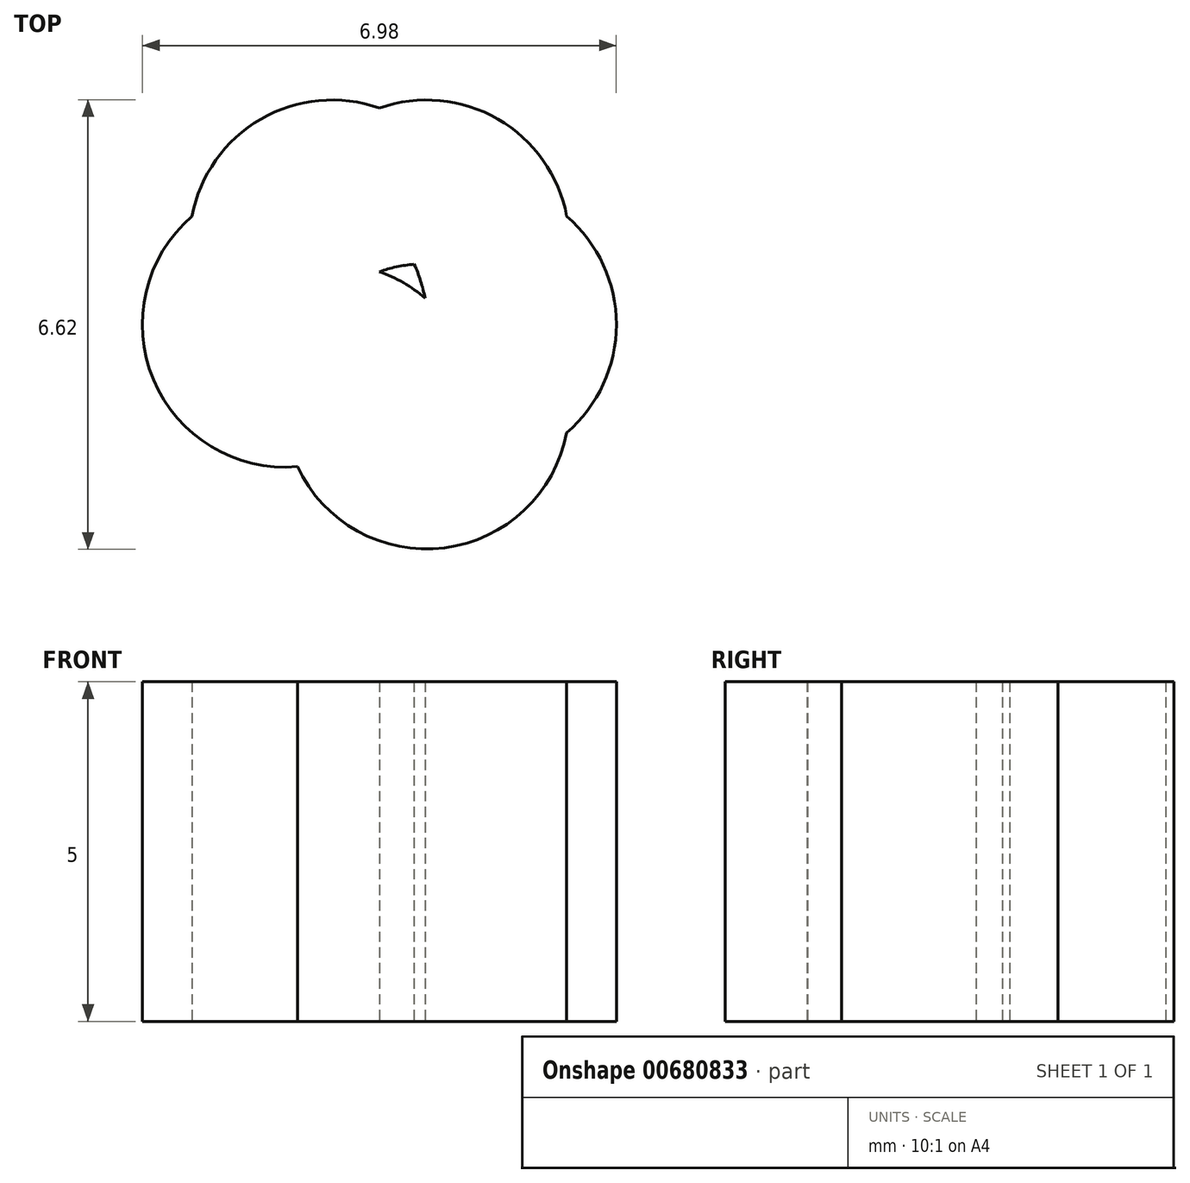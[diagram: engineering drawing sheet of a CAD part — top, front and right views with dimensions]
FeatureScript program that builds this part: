
annotation { "Feature Type Name" : "Feature", "Feature Type Description" : "" }
export const myFeature = defineFeature(function(context is Context, id is Id, definition is map)
    precondition{}
    {
        {
            var Q0;
            Q0=qCreatedBy(makeId("Top.planeOp"),FACE);
            var sketch = newSketch(context, id + "F0", { "sketchPlane" : qUnion([Q0])});
            skCircle(sketch, "E0", {"center": v(0, 0) * mm, "radius": 3.5 * mm});
            skCircle(sketch, "E1", {"center": v(1.4, 0) * mm, "radius": 2.1 * mm});
            skCircle(sketch, "E2.1.0", {"center": v(0.7, 1.2) * mm, "radius": 2.1 * mm});
            skCircle(sketch, "E2.2.0", {"center": v(-0.7, 1.2) * mm, "radius": 2.1 * mm});
            skCircle(sketch, "E2.3.0", {"center": v(-1.4, 0) * mm, "radius": 2.1 * mm});
            skCircle(sketch, "E2.4.0", {"center": v(-0.7, -1.2) * mm, "radius": 2.1 * mm});
            skCircle(sketch, "E2.5.0", {"center": v(0.7, -1.2) * mm, "radius": 2.1 * mm});
            skSolve(sketch);
        }
        {
            var Q0;
            {var subQ0=sQuery(id+"F0.wireOp",EDGE,"E2.2.0");var subQ1=sQuery(id+"F0.wireOp",EDGE,"E1");var subQ2=makeQuery(id+"F0.imprint","INTERSECT",VERTEX,{"disambiguationData":[OD(0.0)],"derivedFrom":[subQ1,subQ0]});Q0=makeQuery(id+"F0.imprint","IMPRINT",FACE,{"disambiguationData":[TD([[makeQuery(id+"F0.imprint","IMPRINT",EDGE,{"disambiguationData":[TD([[subQ2,-1.0]])],"derivedFrom":subQ1}),-1.0]])]});}
            var Q1;
            {var subQ0=sQuery(id+"F0.wireOp",EDGE,"E2.3.0");var subQ1=sQuery(id+"F0.wireOp",EDGE,"E2.1.0");var subQ2=makeQuery(id+"F0.imprint","INTERSECT",VERTEX,{"disambiguationData":[OD(0.0)],"derivedFrom":[subQ1,subQ0]});Q1=makeQuery(id+"F0.imprint","IMPRINT",FACE,{"disambiguationData":[TD([[makeQuery(id+"F0.imprint","IMPRINT",EDGE,{"disambiguationData":[TD([[subQ2,1.0]])],"derivedFrom":subQ1}),-1.0]])]});}
            var Q2;
            {var subQ0=sQuery(id+"F0.wireOp",EDGE,"E2.3.0");var subQ1=sQuery(id+"F0.wireOp",EDGE,"E2.1.0");var subQ2=makeQuery(id+"F0.imprint","INTERSECT",VERTEX,{"disambiguationData":[OD(0.0)],"derivedFrom":[subQ1,subQ0]});Q2=makeQuery(id+"F0.imprint","IMPRINT",FACE,{"disambiguationData":[TD([[makeQuery(id+"F0.imprint","IMPRINT",EDGE,{"disambiguationData":[TD([[subQ2,-1.0]])],"derivedFrom":subQ1}),-1.0]])]});}
            var Q3;
            {var subQ0=sQuery(id+"F0.wireOp",EDGE,"E2.3.0");var subQ1=sQuery(id+"F0.wireOp",EDGE,"E1");var subQ2=makeQuery(id+"F0.imprint","INTERSECT",VERTEX,{"disambiguationData":[OD(0.0)],"derivedFrom":[subQ1,subQ0]});Q3=makeQuery(id+"F0.imprint","IMPRINT",FACE,{"disambiguationData":[TD([[makeQuery(id+"F0.imprint","IMPRINT",EDGE,{"disambiguationData":[TD([[subQ2,-1.0]])],"derivedFrom":subQ1}),-1.0]])]});}
            var Q4;
            {var subQ0=sQuery(id+"F0.wireOp",EDGE,"E2.4.0");var subQ1=sQuery(id+"F0.wireOp",EDGE,"E2.1.0");var subQ2=makeQuery(id+"F0.imprint","INTERSECT",VERTEX,{"disambiguationData":[OD(0.0)],"derivedFrom":[subQ1,subQ0]});Q4=makeQuery(id+"F0.imprint","IMPRINT",FACE,{"disambiguationData":[TD([[makeQuery(id+"F0.imprint","IMPRINT",EDGE,{"disambiguationData":[TD([[subQ2,-1.0]])],"derivedFrom":subQ1}),-1.0]])]});}
            var Q5;
            {var subQ0=sQuery(id+"F0.wireOp",EDGE,"E2.4.0");var subQ1=sQuery(id+"F0.wireOp",EDGE,"E2.2.0");var subQ2=makeQuery(id+"F0.imprint","INTERSECT",VERTEX,{"disambiguationData":[OD(0.0)],"derivedFrom":[subQ1,subQ0]});Q5=makeQuery(id+"F0.imprint","IMPRINT",FACE,{"disambiguationData":[TD([[makeQuery(id+"F0.imprint","IMPRINT",EDGE,{"disambiguationData":[TD([[subQ2,1.0]])],"derivedFrom":subQ1}),-1.0]])]});}
            var Q6;
            {var subQ0=sQuery(id+"F0.wireOp",EDGE,"E2.4.0");var subQ1=sQuery(id+"F0.wireOp",EDGE,"E2.2.0");var subQ2=makeQuery(id+"F0.imprint","INTERSECT",VERTEX,{"disambiguationData":[OD(0.0)],"derivedFrom":[subQ1,subQ0]});Q6=makeQuery(id+"F0.imprint","IMPRINT",FACE,{"disambiguationData":[TD([[makeQuery(id+"F0.imprint","IMPRINT",EDGE,{"disambiguationData":[TD([[subQ2,-1.0]])],"derivedFrom":subQ1}),-1.0]])]});}
            var Q7;
            {var subQ0=sQuery(id+"F0.wireOp",EDGE,"E2.5.0");var subQ1=sQuery(id+"F0.wireOp",EDGE,"E2.3.0");var subQ2=makeQuery(id+"F0.imprint","INTERSECT",VERTEX,{"disambiguationData":[OD(0.0)],"derivedFrom":[subQ1,subQ0]});Q7=makeQuery(id+"F0.imprint","IMPRINT",FACE,{"disambiguationData":[TD([[makeQuery(id+"F0.imprint","IMPRINT",EDGE,{"disambiguationData":[TD([[subQ2,1.0]])],"derivedFrom":subQ1}),-1.0]])]});}
            var Q8;
            {var subQ0=sQuery(id+"F0.wireOp",EDGE,"E2.3.0");var subQ1=sQuery(id+"F0.wireOp",EDGE,"E1");var subQ2=makeQuery(id+"F0.imprint","INTERSECT",VERTEX,{"disambiguationData":[OD(1.0)],"derivedFrom":[subQ1,subQ0]});Q8=makeQuery(id+"F0.imprint","IMPRINT",FACE,{"disambiguationData":[TD([[makeQuery(id+"F0.imprint","IMPRINT",EDGE,{"disambiguationData":[TD([[subQ2,-1.0]])],"derivedFrom":subQ1}),-1.0]])]});}
            var Q9;
            {var subQ0=sQuery(id+"F0.wireOp",EDGE,"E2.2.0");var subQ1=sQuery(id+"F0.wireOp",EDGE,"E1");var subQ2=makeQuery(id+"F0.imprint","INTERSECT",VERTEX,{"disambiguationData":[OD(1.0)],"derivedFrom":[subQ1,subQ0]});Q9=makeQuery(id+"F0.imprint","IMPRINT",FACE,{"disambiguationData":[TD([[makeQuery(id+"F0.imprint","IMPRINT",EDGE,{"disambiguationData":[TD([[subQ2,-1.0]])],"derivedFrom":subQ1}),-1.0]])]});}
            var Q10;
            {var subQ0=sQuery(id+"F0.wireOp",EDGE,"E2.1.0");var subQ1=sQuery(id+"F0.wireOp",EDGE,"E1");var subQ2=makeQuery(id+"F0.imprint","INTERSECT",VERTEX,{"disambiguationData":[OD(1.0)],"derivedFrom":[subQ1,subQ0]});Q10=makeQuery(id+"F0.imprint","IMPRINT",FACE,{"disambiguationData":[TD([[makeQuery(id+"F0.imprint","IMPRINT",EDGE,{"disambiguationData":[TD([[subQ2,-1.0]])],"derivedFrom":subQ1}),-1.0]])]});}
            var Q11;
            {var subQ0=sQuery(id+"F0.wireOp",EDGE,"E2.4.0");var subQ1=sQuery(id+"F0.wireOp",EDGE,"E1");var subQ2=makeQuery(id+"F0.imprint","INTERSECT",VERTEX,{"disambiguationData":[OD(0.0)],"derivedFrom":[subQ1,subQ0]});Q11=makeQuery(id+"F0.imprint","IMPRINT",FACE,{"disambiguationData":[TD([[makeQuery(id+"F0.imprint","IMPRINT",EDGE,{"disambiguationData":[TD([[subQ2,-1.0]])],"derivedFrom":subQ1}),-1.0]])]});}
            var Q12;
            {var subQ7=sQuery(id+"F0.wireOp",EDGE,"E1");var subQ9=sQuery(id+"F0.wireOp",EDGE,"E2.5.0");var subQ10=makeQuery(id+"F0.imprint","INTERSECT",VERTEX,{"disambiguationData":[OD(0.0)],"derivedFrom":[subQ7,subQ9]});Q12=makeQuery(id+"F0.imprint","IMPRINT",FACE,{"disambiguationData":[TD([[makeQuery(id+"F0.imprint","IMPRINT",EDGE,{"disambiguationData":[TD([[subQ10,-1.0]])],"derivedFrom":subQ7}),1.0]])]});}
            var Q13;
            {var subQ0=sQuery(id+"F0.wireOp",EDGE,"E2.3.0");var subQ1=sQuery(id+"F0.wireOp",EDGE,"E1");var subQ2=makeQuery(id+"F0.imprint","INTERSECT",VERTEX,{"disambiguationData":[OD(0.0)],"derivedFrom":[subQ1,subQ0]});Q13=makeQuery(id+"F0.imprint","IMPRINT",FACE,{"disambiguationData":[TD([[makeQuery(id+"F0.imprint","IMPRINT",EDGE,{"disambiguationData":[TD([[subQ2,-1.0]])],"derivedFrom":subQ1}),1.0]])]});}
            var Q14;
            {var subQ0=sQuery(id+"F0.wireOp",EDGE,"E2.2.0");var subQ1=sQuery(id+"F0.wireOp",EDGE,"E1");var subQ2=makeQuery(id+"F0.imprint","INTERSECT",VERTEX,{"disambiguationData":[OD(0.0)],"derivedFrom":[subQ1,subQ0]});Q14=makeQuery(id+"F0.imprint","IMPRINT",FACE,{"disambiguationData":[TD([[makeQuery(id+"F0.imprint","IMPRINT",EDGE,{"disambiguationData":[TD([[subQ2,-1.0]])],"derivedFrom":subQ1}),1.0]])]});}
            var Q15;
            {var subQ0=sQuery(id+"F0.wireOp",EDGE,"E2.2.0");var subQ1=sQuery(id+"F0.wireOp",EDGE,"E1");var subQ2=makeQuery(id+"F0.imprint","INTERSECT",VERTEX,{"disambiguationData":[OD(0.0)],"derivedFrom":[subQ1,subQ0]});Q15=makeQuery(id+"F0.imprint","IMPRINT",FACE,{"disambiguationData":[TD([[makeQuery(id+"F0.imprint","IMPRINT",EDGE,{"disambiguationData":[TD([[subQ2,1.0]])],"derivedFrom":subQ1}),-1.0]])]});}
            var Q16;
            {var subQ0=sQuery(id+"F0.wireOp",EDGE,"E2.2.0");var subQ1=sQuery(id+"F0.wireOp",EDGE,"E1");var subQ2=makeQuery(id+"F0.imprint","INTERSECT",VERTEX,{"disambiguationData":[OD(0.0)],"derivedFrom":[subQ1,subQ0]});Q16=makeQuery(id+"F0.imprint","IMPRINT",FACE,{"disambiguationData":[TD([[makeQuery(id+"F0.imprint","IMPRINT",EDGE,{"disambiguationData":[TD([[subQ2,1.0]])],"derivedFrom":subQ1}),1.0]])]});}
            var Q17;
            {var subQ0=sQuery(id+"F0.wireOp",EDGE,"E2.1.0");var subQ1=sQuery(id+"F0.wireOp",EDGE,"E1");var subQ2=makeQuery(id+"F0.imprint","INTERSECT",VERTEX,{"disambiguationData":[OD(0.0)],"derivedFrom":[subQ1,subQ0]});Q17=makeQuery(id+"F0.imprint","IMPRINT",FACE,{"disambiguationData":[TD([[makeQuery(id+"F0.imprint","IMPRINT",EDGE,{"disambiguationData":[TD([[subQ2,1.0]])],"derivedFrom":subQ1}),1.0]])]});}
            var Q18;
            {var subQ0=sQuery(id+"F0.wireOp",EDGE,"E2.4.0");var subQ1=sQuery(id+"F0.wireOp",EDGE,"E1");var subQ2=makeQuery(id+"F0.imprint","INTERSECT",VERTEX,{"disambiguationData":[OD(1.0)],"derivedFrom":[subQ1,subQ0]});Q18=makeQuery(id+"F0.imprint","IMPRINT",FACE,{"disambiguationData":[TD([[makeQuery(id+"F0.imprint","IMPRINT",EDGE,{"disambiguationData":[TD([[subQ2,-1.0]])],"derivedFrom":subQ1}),1.0]])]});}
            var Q19;
            {var subQ0=sQuery(id+"F0.wireOp",EDGE,"E2.4.0");var subQ1=sQuery(id+"F0.wireOp",EDGE,"E1");var subQ2=makeQuery(id+"F0.imprint","INTERSECT",VERTEX,{"disambiguationData":[OD(1.0)],"derivedFrom":[subQ1,subQ0]});Q19=makeQuery(id+"F0.imprint","IMPRINT",FACE,{"disambiguationData":[TD([[makeQuery(id+"F0.imprint","IMPRINT",EDGE,{"disambiguationData":[TD([[subQ2,-1.0]])],"derivedFrom":subQ1}),-1.0]])]});}
            var Q20;
            {var subQ0=sQuery(id+"F0.wireOp",EDGE,"E2.3.0");var subQ1=sQuery(id+"F0.wireOp",EDGE,"E1");var subQ2=makeQuery(id+"F0.imprint","INTERSECT",VERTEX,{"disambiguationData":[OD(1.0)],"derivedFrom":[subQ1,subQ0]});Q20=makeQuery(id+"F0.imprint","IMPRINT",FACE,{"disambiguationData":[TD([[makeQuery(id+"F0.imprint","IMPRINT",EDGE,{"disambiguationData":[TD([[subQ2,-1.0]])],"derivedFrom":subQ1}),1.0]])]});}
            var Q21;
            {var subQ0=sQuery(id+"F0.wireOp",EDGE,"E2.3.0");var subQ1=sQuery(id+"F0.wireOp",EDGE,"E2.1.0");var subQ2=makeQuery(id+"F0.imprint","INTERSECT",VERTEX,{"disambiguationData":[OD(1.0)],"derivedFrom":[subQ1,subQ0]});Q21=makeQuery(id+"F0.imprint","IMPRINT",FACE,{"disambiguationData":[TD([[makeQuery(id+"F0.imprint","IMPRINT",EDGE,{"disambiguationData":[TD([[subQ2,-1.0]])],"derivedFrom":subQ1}),1.0]])]});}
            var Q22;
            {var subQ0=sQuery(id+"F0.wireOp",EDGE,"E2.4.0");var subQ1=sQuery(id+"F0.wireOp",EDGE,"E2.1.0");var subQ2=makeQuery(id+"F0.imprint","INTERSECT",VERTEX,{"disambiguationData":[OD(1.0)],"derivedFrom":[subQ1,subQ0]});Q22=makeQuery(id+"F0.imprint","IMPRINT",FACE,{"disambiguationData":[TD([[makeQuery(id+"F0.imprint","IMPRINT",EDGE,{"disambiguationData":[TD([[subQ2,-1.0]])],"derivedFrom":subQ1}),1.0]])]});}
            var Q23;
            {var subQ0=sQuery(id+"F0.wireOp",EDGE,"E2.4.0");var subQ1=sQuery(id+"F0.wireOp",EDGE,"E2.2.0");var subQ2=makeQuery(id+"F0.imprint","INTERSECT",VERTEX,{"disambiguationData":[OD(1.0)],"derivedFrom":[subQ1,subQ0]});Q23=makeQuery(id+"F0.imprint","IMPRINT",FACE,{"disambiguationData":[TD([[makeQuery(id+"F0.imprint","IMPRINT",EDGE,{"disambiguationData":[TD([[subQ2,-1.0]])],"derivedFrom":subQ1}),1.0]])]});}
            var Q24;
            {var subQ0=sQuery(id+"F0.wireOp",EDGE,"E2.2.0");var subQ1=sQuery(id+"F0.wireOp",EDGE,"E1");var subQ2=makeQuery(id+"F0.imprint","INTERSECT",VERTEX,{"disambiguationData":[OD(1.0)],"derivedFrom":[subQ1,subQ0]});Q24=makeQuery(id+"F0.imprint","IMPRINT",FACE,{"disambiguationData":[TD([[makeQuery(id+"F0.imprint","IMPRINT",EDGE,{"disambiguationData":[TD([[subQ2,-1.0]])],"derivedFrom":subQ1}),1.0]])]});}
            var Q25;
            {var subQ0=sQuery(id+"F0.wireOp",EDGE,"E2.1.0");var subQ1=sQuery(id+"F0.wireOp",EDGE,"E1");var subQ2=makeQuery(id+"F0.imprint","INTERSECT",VERTEX,{"disambiguationData":[OD(1.0)],"derivedFrom":[subQ1,subQ0]});Q25=makeQuery(id+"F0.imprint","IMPRINT",FACE,{"disambiguationData":[TD([[makeQuery(id+"F0.imprint","IMPRINT",EDGE,{"disambiguationData":[TD([[subQ2,-1.0]])],"derivedFrom":subQ1}),1.0]])]});}
            var Q26;
            {var subQ0=sQuery(id+"F0.wireOp",EDGE,"E2.5.0");var subQ1=sQuery(id+"F0.wireOp",EDGE,"E1");var subQ2=makeQuery(id+"F0.imprint","INTERSECT",VERTEX,{"disambiguationData":[OD(0.0)],"derivedFrom":[subQ1,subQ0]});Q26=makeQuery(id+"F0.imprint","IMPRINT",FACE,{"disambiguationData":[TD([[makeQuery(id+"F0.imprint","IMPRINT",EDGE,{"disambiguationData":[TD([[subQ2,-1.0]])],"derivedFrom":subQ1}),-1.0]])]});}
            var Q27;
            {var subQ0=sQuery(id+"F0.wireOp",EDGE,"E2.4.0");var subQ1=sQuery(id+"F0.wireOp",EDGE,"E1");var subQ2=makeQuery(id+"F0.imprint","INTERSECT",VERTEX,{"disambiguationData":[OD(0.0)],"derivedFrom":[subQ1,subQ0]});Q27=makeQuery(id+"F0.imprint","IMPRINT",FACE,{"disambiguationData":[TD([[makeQuery(id+"F0.imprint","IMPRINT",EDGE,{"disambiguationData":[TD([[subQ2,-1.0]])],"derivedFrom":subQ1}),1.0]])]});}
            var Q28;
            {var subQ0=sQuery(id+"F0.wireOp",EDGE,"E2.4.0");var subQ1=sQuery(id+"F0.wireOp",EDGE,"E2.3.0");var subQ2=makeQuery(id+"F0.imprint","INTERSECT",VERTEX,{"disambiguationData":[OD(1.0)],"derivedFrom":[subQ1,subQ0]});Q28=makeQuery(id+"F0.imprint","IMPRINT",FACE,{"disambiguationData":[TD([[makeQuery(id+"F0.imprint","IMPRINT",EDGE,{"disambiguationData":[TD([[subQ2,-1.0]])],"derivedFrom":subQ1}),1.0]])]});}
            var Q29;
            {var subQ0=sQuery(id+"F0.wireOp",EDGE,"E2.3.0");var subQ1=sQuery(id+"F0.wireOp",EDGE,"E2.2.0");var subQ2=makeQuery(id+"F0.imprint","INTERSECT",VERTEX,{"disambiguationData":[OD(1.0)],"derivedFrom":[subQ1,subQ0]});Q29=makeQuery(id+"F0.imprint","IMPRINT",FACE,{"disambiguationData":[TD([[makeQuery(id+"F0.imprint","IMPRINT",EDGE,{"disambiguationData":[TD([[subQ2,-1.0]])],"derivedFrom":subQ1}),1.0]])]});}
            var Q30;
            {var subQ0=sQuery(id+"F0.wireOp",EDGE,"E2.2.0");var subQ1=sQuery(id+"F0.wireOp",EDGE,"E2.1.0");var subQ2=makeQuery(id+"F0.imprint","INTERSECT",VERTEX,{"disambiguationData":[OD(1.0)],"derivedFrom":[subQ1,subQ0]});Q30=makeQuery(id+"F0.imprint","IMPRINT",FACE,{"disambiguationData":[TD([[makeQuery(id+"F0.imprint","IMPRINT",EDGE,{"disambiguationData":[TD([[subQ2,-1.0]])],"derivedFrom":subQ1}),1.0]])]});}
            extrude(context, id + "F1", {"entities" : qUnion([Q0, Q1, Q2, Q3, Q4, Q5, Q6, Q7, Q8, Q9, Q10, Q11, Q12, Q13, Q14, Q15, Q16, Q17, Q18, Q19, Q20, Q21, Q22, Q23, Q24, Q25, Q26, Q27, Q28, Q29, Q30]), "depth" : 5 * mm, "offsetDistance" : 25 * mm});
        }
    });
